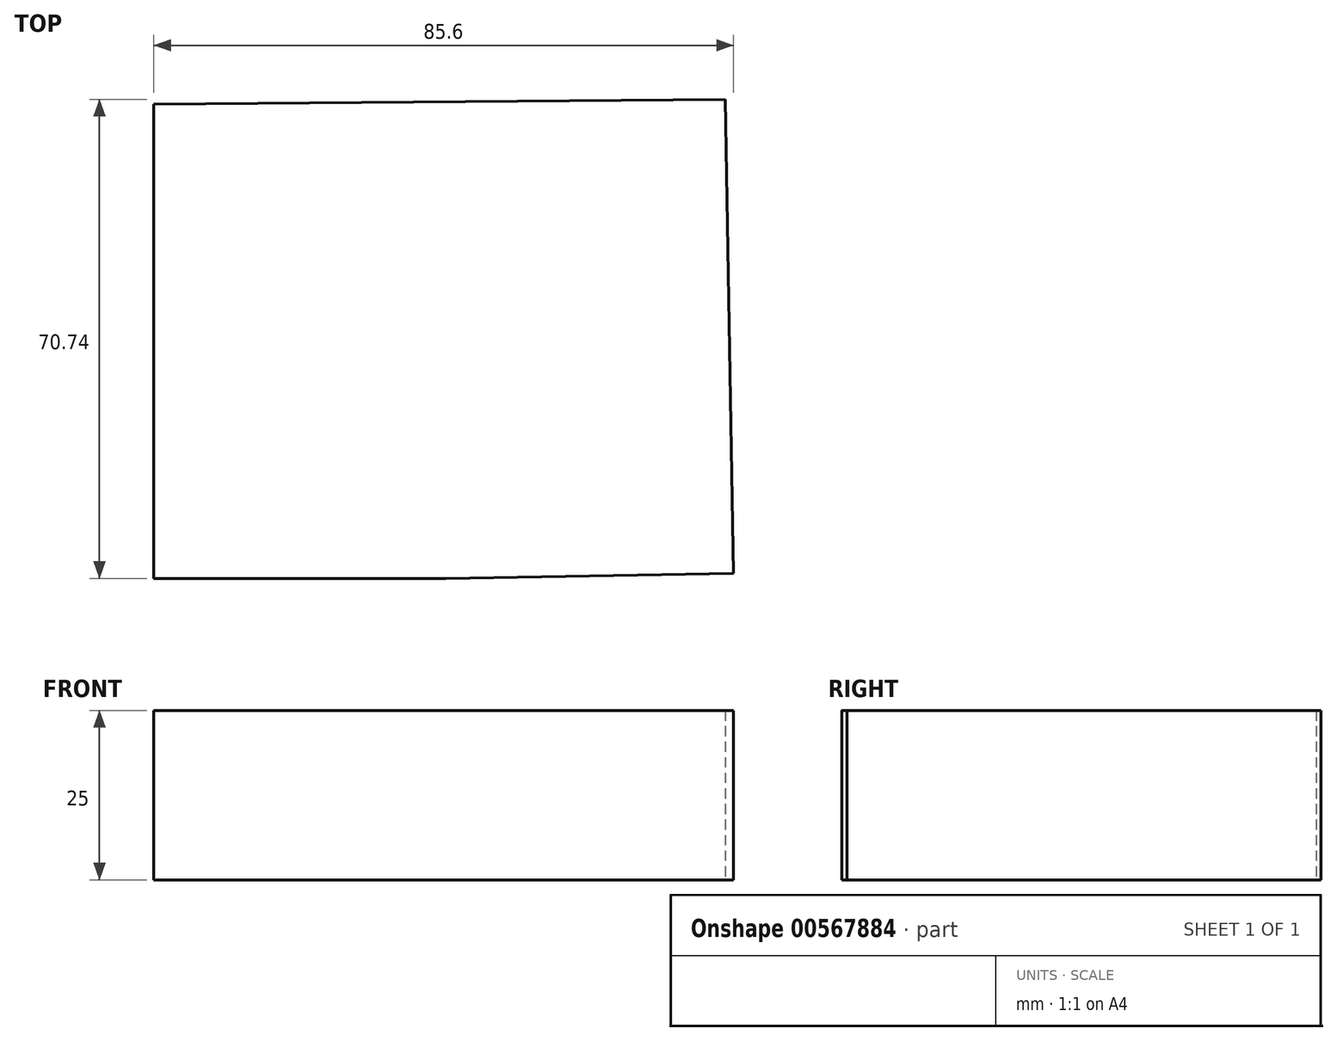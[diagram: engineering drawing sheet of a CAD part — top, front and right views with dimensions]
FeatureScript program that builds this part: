
annotation { "Feature Type Name" : "Feature", "Feature Type Description" : "" }
export const myFeature = defineFeature(function(context is Context, id is Id, definition is map)
    precondition{}
    {
        {
            var Q0;
            Q0=qCreatedBy(makeId("Top.planeOp"),FACE);
            var sketch = newSketch(context, id + "F0", { "sketchPlane" : qUnion([Q0])});
            skLineSegment(sketch, "E0.bottom", {"start": v(2.5, -35) * mm, "end": v(-2.5, -35) * mm});
            skLineSegment(sketch, "E0.top", {"start": v(2.5, 35) * mm, "end": v(-2.5, 35) * mm});
            skLineSegment(sketch, "E0.left", {"start": v(2.5, -35) * mm, "end": v(2.5, 35) * mm});
            skLineSegment(sketch, "E0.right", {"start": v(-2.5, -35) * mm, "end": v(-2.5, 35) * mm});
            skCircle(sketch, "E1", {"center": v(45, 0) * mm, "radius": 40 * mm, "construction": true});
            skCircle(sketch, "E2", {"center": v(45, 0) * mm, "radius": 35 * mm});
            skLineSegment(sketch, "E3", {"start": v(45, 0) * mm, "end": v(134.99, 1.57) * mm, "construction": true});
            skCircle(sketch, "E4", {"center": v(134.99, 1.57) * mm, "radius": 40 * mm, "construction": true});
            skCircle(sketch, "E5", {"center": v(134.99, 1.57) * mm, "radius": 35 * mm});
            skLineSegment(sketch, "E6", {"start": v(0, 0) * mm, "end": v(96.28, 0) * mm, "construction": true});
            skLineSegment(sketch, "E7", {"start": v(134.99, 1.57) * mm, "end": v(224.97, 3.14) * mm, "construction": true});
            skCircle(sketch, "E8", {"center": v(224.97, 3.14) * mm, "radius": 35 * mm});
            skCircle(sketch, "E9", {"center": v(224.97, 3.14) * mm, "radius": 40 * mm, "construction": true});
            skPoint(sketch, "E10", {"position": v(179.98, 2.36) * mm});
            skLineSegment(sketch, "E11", {"start": v(181.87, 37.4) * mm, "end": v(183.09, -32.6) * mm});
            skPoint(sketch, "E12", {"position": v(182.48, 2.4) * mm});
            skLineSegment(sketch, "E13", {"start": v(176.87, 37.3) * mm, "end": v(178.1, -32.68) * mm});
            skPoint(sketch, "E14", {"position": v(177.48, 2.31) * mm});
            skLineSegment(sketch, "E15", {"start": v(177.48, 2.31) * mm, "end": v(182.48, 2.4) * mm});
            skLineSegment(sketch, "E16", {"start": v(86.88, 35.74) * mm, "end": v(88.1, -34.25) * mm});
            skLineSegment(sketch, "E17", {"start": v(91.88, 35.82) * mm, "end": v(93.1, -34.17) * mm});
            skLineSegment(sketch, "E18", {"start": v(92.5, 0.83) * mm, "end": v(87.5, 0.74) * mm});
            skPoint(sketch, "E19", {"position": v(90, 0.79) * mm});
            skPoint(sketch, "E20", {"position": v(87.5, 0.74) * mm});
            skLineSegment(sketch, "E21", {"start": v(2.5, 35) * mm, "end": v(86.88, 35.74) * mm});
            skLineSegment(sketch, "E22", {"start": v(2.5, -35) * mm, "end": v(45, -35) * mm});
            skLineSegment(sketch, "E23", {"start": v(88.1, -34.25) * mm, "end": v(45.61, -35) * mm});
            skLineSegment(sketch, "E24", {"start": v(0, 35) * mm, "end": v(0, -35) * mm});
            skPoint(sketch, "E25", {"position": v(0, 0) * mm});
            skLineSegment(sketch, "E26", {"start": v(86.88, 35.74) * mm, "end": v(44.39, 35) * mm, "construction": true});
            skSolve(sketch);
        }
        {
            var Q0;
            Q0=makeQuery(id+"F0.imprint","IMPRINT",FACE,{"disambiguationData":[TD([[makeQuery(id+"F0.imprint","IMPRINT",EDGE,{"derivedFrom":sQuery(id+"F0.wireOp",EDGE,"E0.left")}),-1.0]])]});
            var Q1;
            {var subQ0=sQuery(id+"F0.wireOp",EDGE,"E2");var subQ1=makeQuery(id+"F0.imprint","INTERSECT",VERTEX,{"derivedFrom":[subQ0,sQuery(id+"F0.wireOp",EDGE,"E22")]});Q1=makeQuery(id+"F0.imprint","IMPRINT",FACE,{"disambiguationData":[TD([[makeQuery(id+"F0.imprint","IMPRINT",EDGE,{"disambiguationData":[TD([[subQ1,1.0]])],"derivedFrom":subQ0}),1.0]])]});}
            extrude(context, id + "F1", {"entities" : qUnion([Q0, Q1]), "depth" : 25 * mm, "offsetDistance" : 25 * mm});
        }
    });
